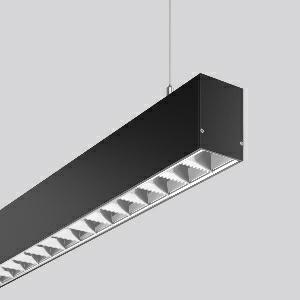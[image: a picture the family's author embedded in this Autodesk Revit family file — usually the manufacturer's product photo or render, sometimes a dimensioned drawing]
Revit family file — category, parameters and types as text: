
# Revit family: less_is_more_50_312335_003_1_76_17fa
name_source: partatom
category: Lighting Fixtures
units: mm (PartAtom-declared; Revit-internal decimal feet)

## family parameters
Cut with Voids When Loaded = No
Host = Face
Light Source = No
Part Type = Normal
Room Calculation Point = No
Round Connector Dimension = Use Diameter
Shared = No

## types (1)
- LESS IS MORE 50 (1 x LED Modul 840, 2650 lm, 4000)
    Apparent Load = 22 VA
    CIE Flux Codes = 95 100 100 100 100
    Color Rendering = 80
    Color Temperature = 4000
    Default Elevation = 1800 mm
    Description = Series: LESS IS MORE 50
Linear pendant luminaire for aesthetically sophisticated lighting. Housing: extruded aluminium profile, powder-coated. End cap aluminium powder-coated. Canopy made of aluminium, powder-coated. Alea optical system: Reflector structure (ABS, Aluminium-coated, highly polished) with integrated diffuser made of non-yellowing plastic (PMMA) opal for glare-free light at the workstation (screen-compliant according to EN 12464-1). Direct light emission. Suitable for pendant. 2-point steel cable suspension freely positionable and infinitely height-adjustable. Special lengths available on request. LED unit with integrated converter interchangeable and removable. Suitable for through-wiring. With sensors or as a safety luminaire on request. 
Colour: deep black, matt (RAL 9005)
Length: 847 mm
Width: 57 mm
Height: 75 mm
Suspension length: 2000 mm
Lamp: LED
Socket: without socket
Colour temperature: 4000K
Colour rendering index (CRI): 80
System power: 22 W
Rated luminous flux: 2650 lm
Luminous efficiency: 120 lm/W
Control gear: Converter, dimmable, DALI
Protection class: I
Type of protection: IP 20
    Height = 75 mm
    Lamp = 1 x LED Modul 840
    Lamp Light Flux = 2650 lm
    Lamp count = 1
    Length = 847 mm
    Lifetime = 50000 h
    Luminous efficacy = 120 lm/W
    Manufacturer = RZB
    ModVariant = No
    Model = 312335.003.1.76
    Mounting Place = Ceiling
    Mounting Type = Pendant
    Number of Poles = 1
    OnlyDefault = Yes
    Power Factor = 1
    Product Name = LESS IS MORE 50
    Product group = Pendant LED linear luminaires
    ProductGroupID = 907
    Protection Class = Protection class I
    Protection Degree = IP 20
    RLX_Detail_Level = 1
    RLX_Emergency_Light_Flux = 0 lm
    RLX_Emergency_Type = 0
    RLX_Emergency_Type_DB = No
    RlxData = <blob elided: 39533 chars, md5=21c0c97c>
    Socket = socket
    Standby Power = 0 W
    System Light Flux = 2650 lm
    System Power = 22 W
    Type Comments = Product without accessories
    Type Image = 312342.003.jpg
    URL = http://relux.com
    VarID = ---
    Voltage = 230 V
    Voltage Range = 220-240 V
    Weight = 0.00 kg
    Width = 57 mm

## geometry (parser evidence)
native form markers: Blend x4, Sweep x13
no freeform markers — native parametric forms only
